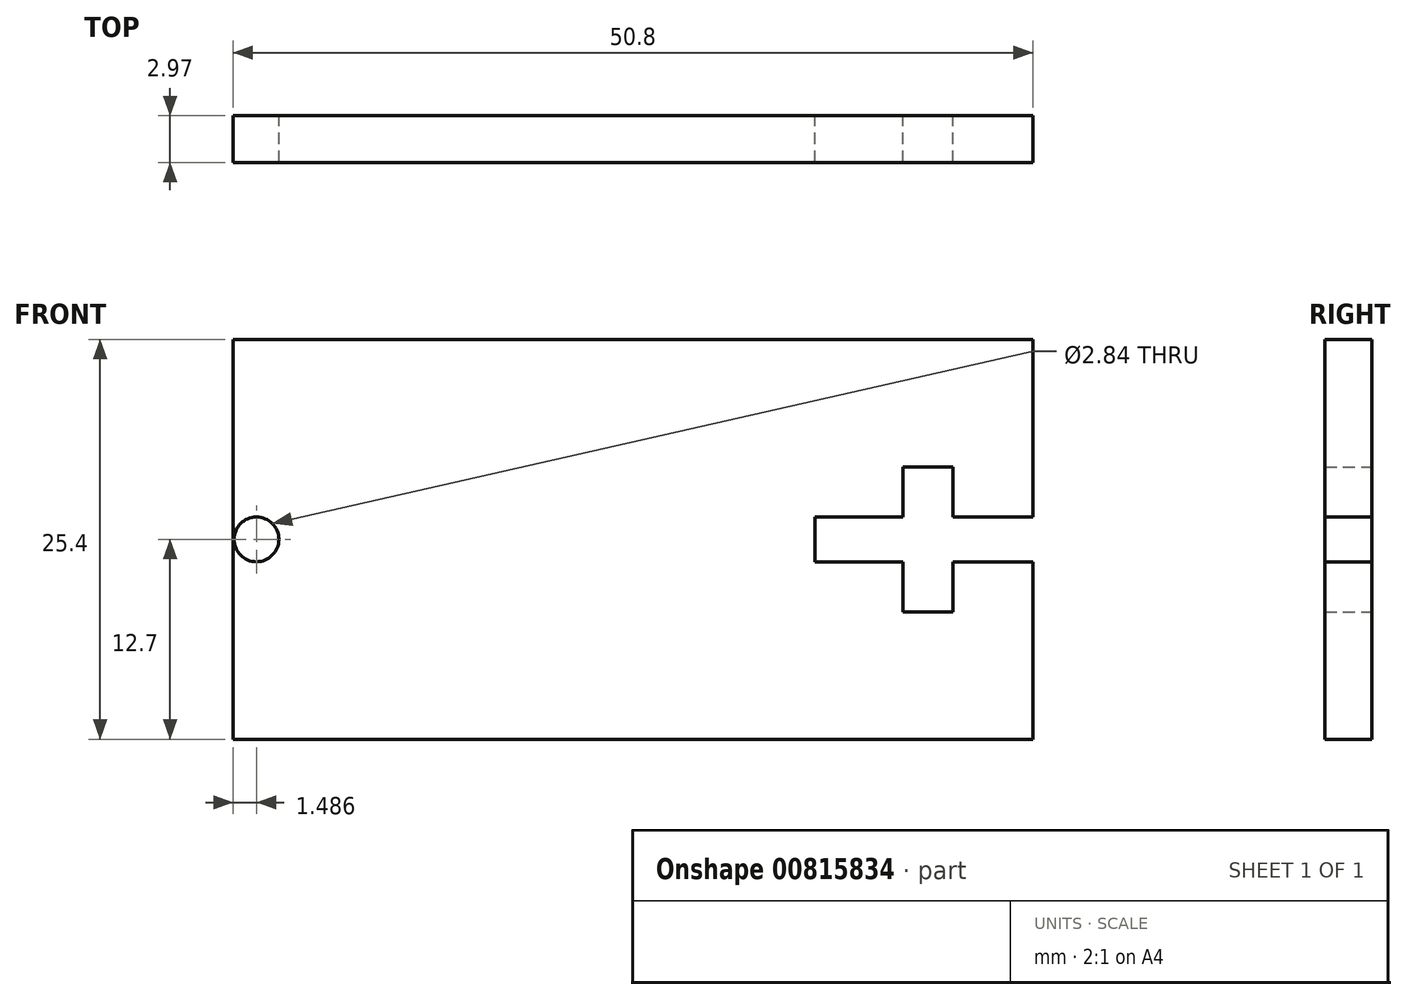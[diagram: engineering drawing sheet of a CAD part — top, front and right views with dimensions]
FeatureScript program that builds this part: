
annotation { "Feature Type Name" : "Feature", "Feature Type Description" : "" }
export const myFeature = defineFeature(function(context is Context, id is Id, definition is map)
    precondition{}
    {
        {
            var Q0;
            Q0=qCreatedBy(makeId("Front.planeOp"),FACE);
            var sketch = newSketch(context, id + "F0", { "sketchPlane" : qUnion([Q0])});
            skLineSegment(sketch, "E0", {"start": v(0, 0) * mm, "end": v(0, 25.4) * mm});
            skLineSegment(sketch, "E1", {"start": v(0, 25.4) * mm, "end": v(50.8, 25.4) * mm});
            skLineSegment(sketch, "E2", {"start": v(50.8, 25.4) * mm, "end": v(50.8, 0) * mm});
            skLineSegment(sketch, "E3", {"start": v(50.8, 0) * mm, "end": v(0, 0) * mm});
            skLineSegment(sketch, "E4", {"start": v(50.8, 14.12) * mm, "end": v(45.72, 14.12) * mm});
            skLineSegment(sketch, "E5", {"start": v(50.8, 11.28) * mm, "end": v(45.72, 11.28) * mm});
            skLineSegment(sketch, "E6", {"start": v(45.72, 14.12) * mm, "end": v(45.72, 17.3) * mm});
            skLineSegment(sketch, "E7", {"start": v(45.72, 17.3) * mm, "end": v(42.55, 17.3) * mm});
            skLineSegment(sketch, "E8", {"start": v(42.55, 17.3) * mm, "end": v(42.55, 14.12) * mm});
            skLineSegment(sketch, "E9", {"start": v(42.55, 14.12) * mm, "end": v(36.96, 14.12) * mm});
            skLineSegment(sketch, "E10", {"start": v(36.96, 14.12) * mm, "end": v(36.96, 11.28) * mm});
            skLineSegment(sketch, "E11", {"start": v(36.96, 11.28) * mm, "end": v(42.55, 11.28) * mm});
            skLineSegment(sketch, "E12", {"start": v(42.55, 11.28) * mm, "end": v(42.55, 8.1) * mm});
            skLineSegment(sketch, "E13", {"start": v(42.55, 8.1) * mm, "end": v(45.72, 8.1) * mm});
            skLineSegment(sketch, "E14", {"start": v(45.72, 8.1) * mm, "end": v(45.72, 11.28) * mm});
            skCircle(sketch, "E15", {"center": v(1.49, 12.7) * mm, "radius": 1.42 * mm});
            skSolve(sketch);
        }
        {
            var Q0;
            Q0=makeQuery(id+"F0.imprint","IMPRINT",FACE,{"disambiguationData":[TD([[makeQuery(id+"F0.imprint","IMPRINT",EDGE,{"derivedFrom":sQuery(id+"F0.wireOp",EDGE,"E0")}),-1.0]])]});
            extrude(context, id + "F1", {"entities" : qUnion([Q0]), "depth" : 2.97 * mm, "offsetDistance" : 25.4 * mm});
        }
    });
